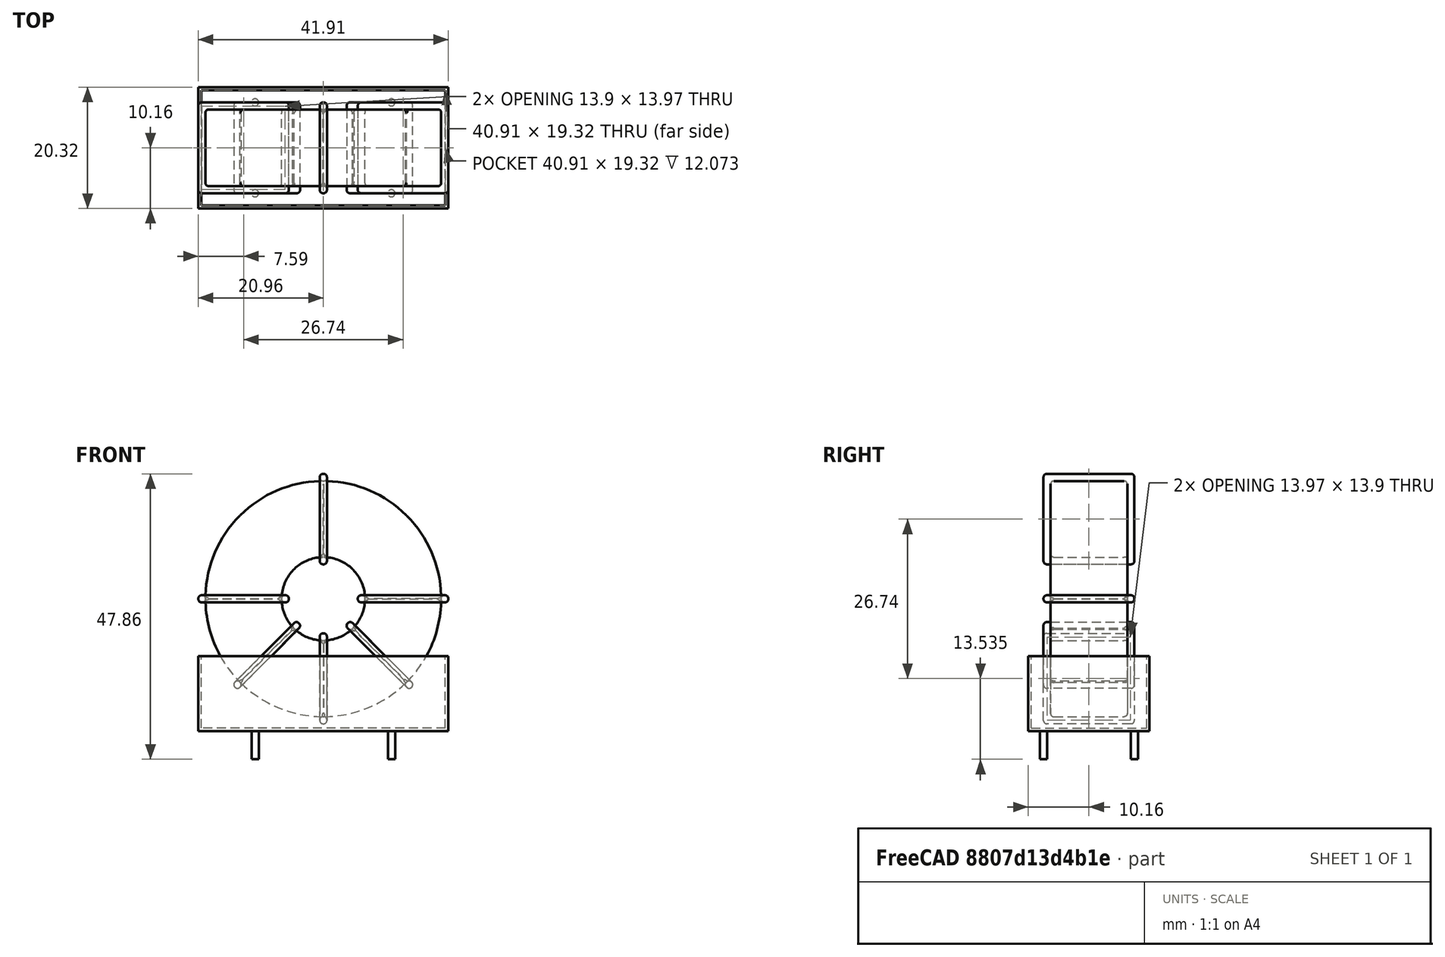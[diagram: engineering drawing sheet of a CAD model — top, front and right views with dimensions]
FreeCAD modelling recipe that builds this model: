
FCSTD DOCUMENT  (FreeCAD 0.16R6712 (Git))
Label: L_CommonMode_Toroid_Vertical_L41.9mm_W20.3mm_Px15.24mm_Py22.86mm_Bourns_8100
License: All rights reserved
LicenseURL: http://en.wikipedia.org/wiki/All_rights_reserved
objects: Sketcher::SketchObject×8, PartDesign::Pad×8, PartDesign::Fillet×5, Spreadsheet::Sheet×1, Part::MultiFuse×1
note: 30 computed .brp shape members not serialized (recipe doc carries the construction recipe); baked Part::Feature solids carry a one-line shape summary decoded from their .brp

FEATURE [Spreadsheet::Sheet] Spreadsheet  label="dimensions"
  cells = A1=Wx; B1(Wx)=41.91; C1(WW)=13.97; D1(iWx)=41.91; A2=Wy; B2(Wy)=15.24; D2(iWy)=20.32; A3=RM; B3(RMx)=15.24; C3(RMy)=22.86; A4=d_wire; B4(d_wire)=1.2; A5=H; B5(H)=31; A6=offsetx; B6(offsetx)=9.524999999999999
FEATURE [Sketcher::SketchObject] Sketch
  Placement = pos=(11.43,-7.62,0) rot=(1,0,0;1.5708rad)
  expr: Placement.Base.x = Spreadsheet.RMy / 2
  expr: Constraints[4] = Spreadsheet.WW / 2
  expr: Placement.Base.y = -Spreadsheet.RMx / 2
  expr: Constraints[0] = Spreadsheet.Wx / 2 - Spreadsheet.d_wire
  expr: Constraints[2] = Spreadsheet.Wx / 2 + Spreadsheet.d_wire + 0.5
  sketch-geometry (2):
    g0: Circle CenterX=0 CenterY=22.655 CenterZ=0 NormalX=0 NormalY=0 NormalZ=1 Radius=19.755
    g1: Circle CenterX=0 CenterY=22.655 CenterZ=0 NormalX=0 NormalY=0 NormalZ=1 Radius=6.985
  constraints (5):
    c: Radius(g0) = 19.755
    c: DistanceX(g-1,g0) = 0
    c: DistanceY(g-1,g0) = 22.655
    c: Coincident(g1,g0)
    c: Radius(g1) = 6.985
FEATURE [PartDesign::Pad] Pad
  Length = 12.84
  Length2 = 100
  Midplane = true
  Placement = pos=(11.43,-7.62,0) rot=(1,0,0;1.5708rad)
  Sketch = -> Sketch
  Type = 0
  expr: Length = Spreadsheet.Wy - 2 * Spreadsheet.d_wire
FEATURE [Sketcher::SketchObject] Sketch001
  Placement = pos=(0,0,0.75) rot=(0,0,1;0rad)
  expr: Constraints[4] = Spreadsheet.RMy
  expr: Constraints[2] = -Spreadsheet.RMx
  expr: Constraints[1] = Spreadsheet.d_wire / 2
  sketch-geometry (4):
    g0: Circle CenterX=0 CenterY=0 CenterZ=0 NormalX=0 NormalY=0 NormalZ=1 Radius=0.6
    g1: Circle CenterX=22.86 CenterY=-15.24 CenterZ=0 NormalX=0 NormalY=0 NormalZ=1 Radius=0.6
    g2: Circle CenterX=0 CenterY=-15.24 CenterZ=0 NormalX=0 NormalY=0 NormalZ=1 Radius=0.6
    g3: Circle CenterX=22.86 CenterY=0 CenterZ=0 NormalX=0 NormalY=0 NormalZ=1 Radius=0.6
  constraints (11):
    c: Equal(g0,g1)
    c: Radius(g0) = 0.6
    c: DistanceY(g-1,g1) = -15.24
    c: Coincident(g0,g-1)
    c: DistanceX(g-1,g1) = 22.86
    c: PointOnObject(g2,g-2)
    c: DistanceY(g-1,g3) = 0
    c: DistanceY(g2,g1) = 0
    c: DistanceX(g3,g1) = 0
    c: Equal(g3,g2)
    c: Equal(g2,g1)
FEATURE [PartDesign::Pad] Pad001
  Length = 5
  Length2 = 0
  Placement = pos=(0,0,0.75) rot=(0,0,1;0rad)
  Reversed = true
  Sketch = -> Sketch001
  Type = 0
FEATURE [PartDesign::Fillet] Fillet
  Base = -> Pad [Edge6,Edge3,Edge2]
  Placement = pos=(11.43,-7.62,0) rot=(1,0,0;1.5708rad)
  Radius = 0.5
FEATURE [Sketcher::SketchObject] Sketch003
  Placement = pos=(11.43,0,22.655) rot=(1,0,0;3.14159rad)
  expr: Placement.Base.x = Spreadsheet.RMy / 2
  expr: Constraints[18] = Spreadsheet.d_wire
  expr: Constraints[16] = Spreadsheet.d_wire
  expr: Constraints[19] = Spreadsheet.d_wire
  expr: Constraints[17] = Spreadsheet.d_wire
  expr: Placement.Base.y = -1 * (Spreadsheet.RMx - Spreadsheet.Wy) / 2
  expr: Constraints[21] = (Spreadsheet.Wx - Spreadsheet.WW) / 2 - Spreadsheet.d_wire
  expr: Constraints[22] = Spreadsheet.Wx / 2 - Spreadsheet.d_wire
  expr: Constraints[43] = Spreadsheet.d_wire
  expr: Constraints[48] = Spreadsheet.Wx - Spreadsheet.d_wire * 2
  expr: Constraints[49] = Spreadsheet.Wy
  expr: Placement.Base.z = Spreadsheet.Wx / 2 + Spreadsheet.d_wire + 0.5
  sketch-geometry (16):
    g0: LineSegment StartX=-5.785 StartY=0 StartZ=0 EndX=-20.955 EndY=0 EndZ=0
    g1: LineSegment StartX=-20.955 StartY=0 StartZ=0 EndX=-20.955 EndY=15.24 EndZ=0
    g2: LineSegment StartX=-20.955 StartY=15.24 StartZ=0 EndX=-5.785 EndY=15.24 EndZ=0
    g3: LineSegment StartX=-5.785 StartY=15.24 StartZ=0 EndX=-5.785 EndY=0 EndZ=0
    g4: LineSegment StartX=-19.755 StartY=14.04 StartZ=0 EndX=-6.985 EndY=14.04 EndZ=0
    g5: LineSegment StartX=-6.985 StartY=14.04 StartZ=0 EndX=-6.985 EndY=1.2 EndZ=0
    g6: LineSegment StartX=-6.985 StartY=1.2 StartZ=0 EndX=-19.755 EndY=1.2 EndZ=0
    g7: LineSegment StartX=-19.755 StartY=1.2 StartZ=0 EndX=-19.755 EndY=14.04 EndZ=0
    g8: LineSegment StartX=5.785 StartY=15.24 StartZ=0 EndX=20.955 EndY=15.24 EndZ=0
    g9: LineSegment StartX=20.955 StartY=15.24 StartZ=0 EndX=20.955 EndY=0 EndZ=0
    g10: LineSegment StartX=20.955 StartY=0 StartZ=0 EndX=5.785 EndY=0 EndZ=0
    g11: LineSegment StartX=5.785 StartY=0 StartZ=0 EndX=5.785 EndY=15.24 EndZ=0
    g12: LineSegment StartX=6.985 StartY=14.04 StartZ=0 EndX=19.755 EndY=14.04 EndZ=0
    g13: LineSegment StartX=19.755 StartY=14.04 StartZ=0 EndX=19.755 EndY=1.2 EndZ=0
    g14: LineSegment StartX=19.755 StartY=1.2 StartZ=0 EndX=6.985 EndY=1.2 EndZ=0
    g15: LineSegment StartX=6.985 StartY=1.2 StartZ=0 EndX=6.985 EndY=14.04 EndZ=0
  constraints (50):
    c: Horizontal(g0)
    c: Coincident(g1,g0)
    c: Vertical(g1)
    c: Coincident(g2,g1)
    c: Horizontal(g2)
    c: Coincident(g3,g2)
    c: Coincident(g3,g0)
    c: Vertical(g3)
    c: Coincident(g4,g5)
    c: Coincident(g5,g6)
    c: Coincident(g6,g7)
    c: Coincident(g7,g4)
    c: Horizontal(g4)
    c: Horizontal(g6)
    c: Vertical(g5)
    c: Vertical(g7)
    c: DistanceX(g1,g4) = 1.2
    c: DistanceY(g4,g1) = 1.2
    c: DistanceX(g5,g0) = 1.2
    c: DistanceY(g0,g5) = 1.2
    c: DistanceY(g-1,g0) = 0
    c: DistanceX(g6,g6) = 12.77
    c: DistanceX(g6,g-1) = 19.755
    c: Coincident(g8,g9)
    c: Coincident(g9,g10)
    c: Coincident(g10,g11)
    c: Coincident(g11,g8)
    c: Horizontal(g8)
    c: Horizontal(g10)
    c: Vertical(g9)
    c: Vertical(g11)
    c: Coincident(g12,g13)
    c: Coincident(g13,g14)
    c: Coincident(g14,g15)
    c: Coincident(g15,g12)
    c: Horizontal(g12)
    c: Horizontal(g14)
    c: Vertical(g13)
    c: Vertical(g15)
    c: DistanceY(g8,g2) = 0
    c: DistanceY(g10,g0) = 0
    c: DistanceY(g14,g5) = 0
    c: DistanceY(g12,g4) = 0
    c: DistanceX(g8,g12) = 1.2
    c: Equal(g8,g2)
    c: Equal(g12,g4)
    c: Equal(g9,g1)
    c: Equal(g13,g7)
    c: DistanceX(g4,g12) = 39.51
    c: DistanceY(g0,g1) = 15.24
FEATURE [PartDesign::Pad] Pad002
  Length = 1.2
  Length2 = 100
  Midplane = true
  Placement = pos=(11.43,0,22.655) rot=(1,0,0;3.14159rad)
  Sketch = -> Sketch003
  Type = 0
  expr: Length = Spreadsheet.d_wire
FEATURE [PartDesign::Fillet] Fillet001
  Base = -> Pad002 [Edge38,Edge41,Edge42,Edge43,Edge29,Edge32,Edge33,Edge34,Edge25,Edge35,Edge36,Edge13,Edge14,Edge15,Edge16,Edge17,Edge18,Edge19,Edge1,Edge2,Edge3,Edge4,Edge5,Edge6,Edge7,Edge37,Edge39,Edge40,Edge20,Edge23,Edge24,Edge21,Edge22,Edge8,Edge9,Edge10,Edge11,Edge12,Edge26,Edge27,+8 more]
  Placement = pos=(11.43,0,22.655) rot=(1,0,0;3.14159rad)
  Radius = 0.564
  expr: Radius = Spreadsheet.d_wire * 0.47
FEATURE [Sketcher::SketchObject] Sketch004
  Placement = pos=(11.43,0,22.655) rot=(0.92388,0,0.382683;3.14159rad)
  expr: Placement.Base.x = Spreadsheet.RMy / 2
  expr: Constraints[18] = Spreadsheet.d_wire
  expr: Constraints[16] = Spreadsheet.d_wire
  expr: Constraints[19] = Spreadsheet.d_wire
  expr: Constraints[17] = Spreadsheet.d_wire
  expr: Placement.Base.y = -1 * (Spreadsheet.RMx - Spreadsheet.Wy) / 2
  expr: Constraints[21] = (Spreadsheet.Wx - Spreadsheet.WW) / 2 - Spreadsheet.d_wire
  expr: Constraints[22] = Spreadsheet.Wx / 2 - Spreadsheet.d_wire
  expr: Constraints[43] = Spreadsheet.d_wire
  expr: Constraints[48] = Spreadsheet.Wx - 2 * Spreadsheet.d_wire
  expr: Constraints[49] = Spreadsheet.Wy
  expr: Placement.Base.z = Spreadsheet.Wx / 2 + Spreadsheet.d_wire + 0.5
  sketch-geometry (16):
    g0: LineSegment StartX=-5.785 StartY=0 StartZ=0 EndX=-20.955 EndY=0 EndZ=0
    g1: LineSegment StartX=-20.955 StartY=0 StartZ=0 EndX=-20.955 EndY=15.24 EndZ=0
    g2: LineSegment StartX=-20.955 StartY=15.24 StartZ=0 EndX=-5.785 EndY=15.24 EndZ=0
    g3: LineSegment StartX=-5.785 StartY=15.24 StartZ=0 EndX=-5.785 EndY=0 EndZ=0
    g4: LineSegment StartX=-19.755 StartY=14.04 StartZ=0 EndX=-6.985 EndY=14.04 EndZ=0
    g5: LineSegment StartX=-6.985 StartY=14.04 StartZ=0 EndX=-6.985 EndY=1.2 EndZ=0
    g6: LineSegment StartX=-6.985 StartY=1.2 StartZ=0 EndX=-19.755 EndY=1.2 EndZ=0
    g7: LineSegment StartX=-19.755 StartY=1.2 StartZ=0 EndX=-19.755 EndY=14.04 EndZ=0
    g8: LineSegment StartX=5.785 StartY=15.24 StartZ=0 EndX=20.955 EndY=15.24 EndZ=0
    g9: LineSegment StartX=20.955 StartY=15.24 StartZ=0 EndX=20.955 EndY=0 EndZ=0
    g10: LineSegment StartX=20.955 StartY=0 StartZ=0 EndX=5.785 EndY=0 EndZ=0
    g11: LineSegment StartX=5.785 StartY=0 StartZ=0 EndX=5.785 EndY=15.24 EndZ=0
    g12: LineSegment StartX=6.985 StartY=14.04 StartZ=0 EndX=19.755 EndY=14.04 EndZ=0
    g13: LineSegment StartX=19.755 StartY=14.04 StartZ=0 EndX=19.755 EndY=1.2 EndZ=0
    g14: LineSegment StartX=19.755 StartY=1.2 StartZ=0 EndX=6.985 EndY=1.2 EndZ=0
    g15: LineSegment StartX=6.985 StartY=1.2 StartZ=0 EndX=6.985 EndY=14.04 EndZ=0
  constraints (50):
    c: Horizontal(g0)
    c: Coincident(g1,g0)
    c: Vertical(g1)
    c: Coincident(g2,g1)
    c: Horizontal(g2)
    c: Coincident(g3,g2)
    c: Coincident(g3,g0)
    c: Vertical(g3)
    c: Coincident(g4,g5)
    c: Coincident(g5,g6)
    c: Coincident(g6,g7)
    c: Coincident(g7,g4)
    c: Horizontal(g4)
    c: Horizontal(g6)
    c: Vertical(g5)
    c: Vertical(g7)
    c: DistanceX(g1,g4) = 1.2
    c: DistanceY(g4,g1) = 1.2
    c: DistanceX(g5,g0) = 1.2
    c: DistanceY(g0,g5) = 1.2
    c: DistanceY(g-1,g0) = 0
    c: DistanceX(g6,g6) = 12.77
    c: DistanceX(g6,g-1) = 19.755
    c: Coincident(g8,g9)
    c: Coincident(g9,g10)
    c: Coincident(g10,g11)
    c: Coincident(g11,g8)
    c: Horizontal(g8)
    c: Horizontal(g10)
    c: Vertical(g9)
    c: Vertical(g11)
    c: Coincident(g12,g13)
    c: Coincident(g13,g14)
    c: Coincident(g14,g15)
    c: Coincident(g15,g12)
    c: Horizontal(g12)
    c: Horizontal(g14)
    c: Vertical(g13)
    c: Vertical(g15)
    c: DistanceY(g8,g2) = 0
    c: DistanceY(g10,g0) = 0
    c: DistanceY(g14,g5) = 0
    c: DistanceY(g12,g4) = 0
    c: DistanceX(g8,g12) = 1.2
    c: Equal(g8,g2)
    c: Equal(g12,g4)
    c: Equal(g9,g1)
    c: Equal(g13,g7)
    c: DistanceX(g4,g12) = 39.51
    c: DistanceY(g0,g1) = 15.24
FEATURE [PartDesign::Pad] Pad003
  Length = 1.2
  Length2 = 100
  Midplane = true
  Placement = pos=(11.43,0,22.655) rot=(0.92388,0,0.382683;3.14159rad)
  Sketch = -> Sketch004
  Type = 0
  expr: Length = Spreadsheet.d_wire
FEATURE [PartDesign::Fillet] Fillet002
  Base = -> Pad003 [Edge38,Edge41,Edge42,Edge43,Edge29,Edge32,Edge33,Edge34,Edge25,Edge35,Edge36,Edge13,Edge14,Edge15,Edge16,Edge17,Edge18,Edge19,Edge1,Edge2,Edge3,Edge4,Edge5,Edge6,Edge7,Edge37,Edge39,Edge40,Edge20,Edge23,Edge24,Edge21,Edge22,Edge8,Edge9,Edge10,Edge11,Edge12,Edge26,Edge27,+8 more]
  Placement = pos=(11.43,0,22.655) rot=(0.92388,0,0.382683;3.14159rad)
  Radius = 0.564
  expr: Radius = Spreadsheet.d_wire * 0.47
FEATURE [Sketcher::SketchObject] Sketch005
  Placement = pos=(11.43,0,22.655) rot=(0.92388,0,-0.382683;3.14159rad)
  expr: Placement.Base.x = Spreadsheet.RMy / 2
  expr: Constraints[18] = Spreadsheet.d_wire
  expr: Constraints[16] = Spreadsheet.d_wire
  expr: Constraints[19] = Spreadsheet.d_wire
  expr: Constraints[17] = Spreadsheet.d_wire
  expr: Placement.Base.y = -1 * (Spreadsheet.RMx - Spreadsheet.Wy) / 2
  expr: Constraints[21] = (Spreadsheet.Wx - Spreadsheet.WW) / 2 - Spreadsheet.d_wire
  expr: Constraints[22] = Spreadsheet.Wx / 2 - Spreadsheet.d_wire
  expr: Constraints[43] = Spreadsheet.d_wire
  expr: Constraints[48] = Spreadsheet.Wx - 2 * Spreadsheet.d_wire
  expr: Constraints[49] = Spreadsheet.Wy
  expr: Placement.Base.z = Spreadsheet.Wx / 2 + Spreadsheet.d_wire + 0.5
  sketch-geometry (16):
    g0: LineSegment StartX=-5.785 StartY=0 StartZ=0 EndX=-20.955 EndY=0 EndZ=0
    g1: LineSegment StartX=-20.955 StartY=0 StartZ=0 EndX=-20.955 EndY=15.24 EndZ=0
    g2: LineSegment StartX=-20.955 StartY=15.24 StartZ=0 EndX=-5.785 EndY=15.24 EndZ=0
    g3: LineSegment StartX=-5.785 StartY=15.24 StartZ=0 EndX=-5.785 EndY=0 EndZ=0
    g4: LineSegment StartX=-19.755 StartY=14.04 StartZ=0 EndX=-6.985 EndY=14.04 EndZ=0
    g5: LineSegment StartX=-6.985 StartY=14.04 StartZ=0 EndX=-6.985 EndY=1.2 EndZ=0
    g6: LineSegment StartX=-6.985 StartY=1.2 StartZ=0 EndX=-19.755 EndY=1.2 EndZ=0
    g7: LineSegment StartX=-19.755 StartY=1.2 StartZ=0 EndX=-19.755 EndY=14.04 EndZ=0
    g8: LineSegment StartX=5.785 StartY=15.24 StartZ=0 EndX=20.955 EndY=15.24 EndZ=0
    g9: LineSegment StartX=20.955 StartY=15.24 StartZ=0 EndX=20.955 EndY=0 EndZ=0
    g10: LineSegment StartX=20.955 StartY=0 StartZ=0 EndX=5.785 EndY=0 EndZ=0
    g11: LineSegment StartX=5.785 StartY=0 StartZ=0 EndX=5.785 EndY=15.24 EndZ=0
    g12: LineSegment StartX=6.985 StartY=14.04 StartZ=0 EndX=19.755 EndY=14.04 EndZ=0
    g13: LineSegment StartX=19.755 StartY=14.04 StartZ=0 EndX=19.755 EndY=1.2 EndZ=0
    g14: LineSegment StartX=19.755 StartY=1.2 StartZ=0 EndX=6.985 EndY=1.2 EndZ=0
    g15: LineSegment StartX=6.985 StartY=1.2 StartZ=0 EndX=6.985 EndY=14.04 EndZ=0
  constraints (50):
    c: Horizontal(g0)
    c: Coincident(g1,g0)
    c: Vertical(g1)
    c: Coincident(g2,g1)
    c: Horizontal(g2)
    c: Coincident(g3,g2)
    c: Coincident(g3,g0)
    c: Vertical(g3)
    c: Coincident(g4,g5)
    c: Coincident(g5,g6)
    c: Coincident(g6,g7)
    c: Coincident(g7,g4)
    c: Horizontal(g4)
    c: Horizontal(g6)
    c: Vertical(g5)
    c: Vertical(g7)
    c: DistanceX(g1,g4) = 1.2
    c: DistanceY(g4,g1) = 1.2
    c: DistanceX(g5,g0) = 1.2
    c: DistanceY(g0,g5) = 1.2
    c: DistanceY(g-1,g0) = 0
    c: DistanceX(g6,g6) = 12.77
    c: DistanceX(g6,g-1) = 19.755
    c: Coincident(g8,g9)
    c: Coincident(g9,g10)
    c: Coincident(g10,g11)
    c: Coincident(g11,g8)
    c: Horizontal(g8)
    c: Horizontal(g10)
    c: Vertical(g9)
    c: Vertical(g11)
    c: Coincident(g12,g13)
    c: Coincident(g13,g14)
    c: Coincident(g14,g15)
    c: Coincident(g15,g12)
    c: Horizontal(g12)
    c: Horizontal(g14)
    c: Vertical(g13)
    c: Vertical(g15)
    c: DistanceY(g8,g2) = 0
    c: DistanceY(g10,g0) = 0
    c: DistanceY(g14,g5) = 0
    c: DistanceY(g12,g4) = 0
    c: DistanceX(g8,g12) = 1.2
    c: Equal(g8,g2)
    c: Equal(g12,g4)
    c: Equal(g9,g1)
    c: Equal(g13,g7)
    c: DistanceX(g4,g12) = 39.51
    c: DistanceY(g0,g1) = 15.24
FEATURE [PartDesign::Pad] Pad004
  Length = 1.2
  Length2 = 100
  Midplane = true
  Placement = pos=(11.43,0,22.655) rot=(0.92388,0,-0.382683;3.14159rad)
  Sketch = -> Sketch005
  Type = 0
  expr: Length = Spreadsheet.d_wire
FEATURE [PartDesign::Fillet] Fillet003
  Base = -> Pad004 [Edge38,Edge41,Edge42,Edge43,Edge29,Edge32,Edge33,Edge34,Edge25,Edge35,Edge36,Edge13,Edge14,Edge15,Edge16,Edge17,Edge18,Edge19,Edge1,Edge2,Edge3,Edge4,Edge5,Edge6,Edge7,Edge37,Edge39,Edge40,Edge20,Edge23,Edge24,Edge21,Edge22,Edge8,Edge9,Edge10,Edge11,Edge12,Edge26,Edge27,+8 more]
  Placement = pos=(11.43,0,22.655) rot=(0.92388,0,-0.382683;3.14159rad)
  Radius = 0.564
  expr: Radius = Spreadsheet.d_wire * 0.47
FEATURE [Sketcher::SketchObject] Sketch006
  Placement = pos=(11.43,0,22.655) rot=(0.707107,0,0.707107;3.14159rad)
  expr: Placement.Base.x = Spreadsheet.RMy / 2
  expr: Constraints[18] = Spreadsheet.d_wire
  expr: Constraints[16] = Spreadsheet.d_wire
  expr: Constraints[19] = Spreadsheet.d_wire
  expr: Constraints[17] = Spreadsheet.d_wire
  expr: Placement.Base.y = -1 * (Spreadsheet.RMx - Spreadsheet.Wy) / 2
  expr: Constraints[21] = (Spreadsheet.Wx - Spreadsheet.WW) / 2 - Spreadsheet.d_wire
  expr: Constraints[22] = Spreadsheet.Wx / 2 - Spreadsheet.d_wire
  expr: Constraints[43] = Spreadsheet.d_wire
  expr: Constraints[48] = Spreadsheet.Wx - Spreadsheet.d_wire * 2
  expr: Constraints[49] = Spreadsheet.Wy
  expr: Placement.Base.z = Spreadsheet.Wx / 2 + Spreadsheet.d_wire + 0.5
  sketch-geometry (16):
    g0: LineSegment StartX=-5.785 StartY=0 StartZ=0 EndX=-20.955 EndY=0 EndZ=0
    g1: LineSegment StartX=-20.955 StartY=0 StartZ=0 EndX=-20.955 EndY=15.24 EndZ=0
    g2: LineSegment StartX=-20.955 StartY=15.24 StartZ=0 EndX=-5.785 EndY=15.24 EndZ=0
    g3: LineSegment StartX=-5.785 StartY=15.24 StartZ=0 EndX=-5.785 EndY=0 EndZ=0
    g4: LineSegment StartX=-19.755 StartY=14.04 StartZ=0 EndX=-6.985 EndY=14.04 EndZ=0
    g5: LineSegment StartX=-6.985 StartY=14.04 StartZ=0 EndX=-6.985 EndY=1.2 EndZ=0
    g6: LineSegment StartX=-6.985 StartY=1.2 StartZ=0 EndX=-19.755 EndY=1.2 EndZ=0
    g7: LineSegment StartX=-19.755 StartY=1.2 StartZ=0 EndX=-19.755 EndY=14.04 EndZ=0
    g8: LineSegment StartX=5.785 StartY=15.24 StartZ=0 EndX=20.955 EndY=15.24 EndZ=0
    g9: LineSegment StartX=20.955 StartY=15.24 StartZ=0 EndX=20.955 EndY=0 EndZ=0
    g10: LineSegment StartX=20.955 StartY=0 StartZ=0 EndX=5.785 EndY=0 EndZ=0
    g11: LineSegment StartX=5.785 StartY=0 StartZ=0 EndX=5.785 EndY=15.24 EndZ=0
    g12: LineSegment StartX=6.985 StartY=14.04 StartZ=0 EndX=19.755 EndY=14.04 EndZ=0
    g13: LineSegment StartX=19.755 StartY=14.04 StartZ=0 EndX=19.755 EndY=1.2 EndZ=0
    g14: LineSegment StartX=19.755 StartY=1.2 StartZ=0 EndX=6.985 EndY=1.2 EndZ=0
    g15: LineSegment StartX=6.985 StartY=1.2 StartZ=0 EndX=6.985 EndY=14.04 EndZ=0
  constraints (50):
    c: Horizontal(g0)
    c: Coincident(g1,g0)
    c: Vertical(g1)
    c: Coincident(g2,g1)
    c: Horizontal(g2)
    c: Coincident(g3,g2)
    c: Coincident(g3,g0)
    c: Vertical(g3)
    c: Coincident(g4,g5)
    c: Coincident(g5,g6)
    c: Coincident(g6,g7)
    c: Coincident(g7,g4)
    c: Horizontal(g4)
    c: Horizontal(g6)
    c: Vertical(g5)
    c: Vertical(g7)
    c: DistanceX(g1,g4) = 1.2
    c: DistanceY(g4,g1) = 1.2
    c: DistanceX(g5,g0) = 1.2
    c: DistanceY(g0,g5) = 1.2
    c: DistanceY(g-1,g0) = 0
    c: DistanceX(g6,g6) = 12.77
    c: DistanceX(g6,g-1) = 19.755
    c: Coincident(g8,g9)
    c: Coincident(g9,g10)
    c: Coincident(g10,g11)
    c: Coincident(g11,g8)
    c: Horizontal(g8)
    c: Horizontal(g10)
    c: Vertical(g9)
    c: Vertical(g11)
    c: Coincident(g12,g13)
    c: Coincident(g13,g14)
    c: Coincident(g14,g15)
    c: Coincident(g15,g12)
    c: Horizontal(g12)
    c: Horizontal(g14)
    c: Vertical(g13)
    c: Vertical(g15)
    c: DistanceY(g8,g2) = 0
    c: DistanceY(g10,g0) = 0
    c: DistanceY(g14,g5) = 0
    c: DistanceY(g12,g4) = 0
    c: DistanceX(g8,g12) = 1.2
    c: Equal(g8,g2)
    c: Equal(g12,g4)
    c: Equal(g9,g1)
    c: Equal(g13,g7)
    c: DistanceX(g4,g12) = 39.51
    c: DistanceY(g0,g1) = 15.24
FEATURE [PartDesign::Pad] Pad005
  Length = 1.2
  Length2 = 100
  Midplane = true
  Placement = pos=(11.43,0,22.655) rot=(0.707107,0,0.707107;3.14159rad)
  Sketch = -> Sketch006
  Type = 0
  expr: Length = Spreadsheet.d_wire
FEATURE [PartDesign::Fillet] Fillet004
  Base = -> Pad005 [Edge38,Edge41,Edge42,Edge43,Edge29,Edge32,Edge33,Edge34,Edge25,Edge35,Edge36,Edge13,Edge14,Edge15,Edge16,Edge17,Edge18,Edge19,Edge1,Edge2,Edge3,Edge4,Edge5,Edge6,Edge7,Edge37,Edge39,Edge40,Edge20,Edge23,Edge24,Edge21,Edge22,Edge8,Edge9,Edge10,Edge11,Edge12,Edge26,Edge27,+8 more]
  Placement = pos=(11.43,0,22.655) rot=(0.707107,0,0.707107;3.14159rad)
  Radius = 0.564
  expr: Radius = Spreadsheet.d_wire * 0.47
FEATURE [Sketcher::SketchObject] Sketch007
  Placement = pos=(11.43,0,0.5) rot=(0,0,1;0rad)
  expr: Placement.Base.x = Spreadsheet.RMy / 2
  expr: Placement.Base.z = 0.5
  expr: Constraints[11] = Spreadsheet.iWx / 2
  expr: Constraints[10] = (Spreadsheet.iWy - Spreadsheet.RMx) / 2
  expr: Constraints[9] = Spreadsheet.iWy
  expr: Constraints[8] = Spreadsheet.iWx
  sketch-geometry (4):
    g0: LineSegment StartX=-20.955 StartY=2.54 StartZ=0 EndX=20.955 EndY=2.54 EndZ=0
    g1: LineSegment StartX=20.955 StartY=2.54 StartZ=0 EndX=20.955 EndY=-17.78 EndZ=0
    g2: LineSegment StartX=20.955 StartY=-17.78 StartZ=0 EndX=-20.955 EndY=-17.78 EndZ=0
    g3: LineSegment StartX=-20.955 StartY=-17.78 StartZ=0 EndX=-20.955 EndY=2.54 EndZ=0
  constraints (12):
    c: Coincident(g0,g1)
    c: Coincident(g1,g2)
    c: Coincident(g2,g3)
    c: Coincident(g3,g0)
    c: Horizontal(g0)
    c: Horizontal(g2)
    c: Vertical(g1)
    c: Vertical(g3)
    c: DistanceX(g0,g0) = 41.91
    c: DistanceY(g3,g3) = 20.32
    c: DistanceY(g-1,g0) = 2.54
    c: DistanceX(g0,g-1) = 20.955
FEATURE [PartDesign::Pad] Pad006
  Length = 0.5
  Length2 = 100
  Placement = pos=(11.43,0,0.5) rot=(0,0,1;0rad)
  Sketch = -> Sketch007
  Type = 0
FEATURE [Sketcher::SketchObject] Sketch008
  Placement = pos=(11.43,0,0.5) rot=(0,0,1;0rad)
  expr: Placement.Base.x = Spreadsheet.RMy / 2
  expr: Constraints[8] = Spreadsheet.iWx
  expr: Constraints[9] = Spreadsheet.iWy
  expr: Constraints[10] = (Spreadsheet.iWy - Spreadsheet.RMx) / 2
  expr: Placement.Base.z = 0.5
  expr: Constraints[21] = 0.5
  expr: Constraints[11] = Spreadsheet.iWx / 2
  sketch-geometry (8):
    g0: LineSegment StartX=-20.955 StartY=2.54 StartZ=0 EndX=20.955 EndY=2.54 EndZ=0
    g1: LineSegment StartX=20.955 StartY=2.54 StartZ=0 EndX=20.955 EndY=-17.78 EndZ=0
    g2: LineSegment StartX=20.955 StartY=-17.78 StartZ=0 EndX=-20.955 EndY=-17.78 EndZ=0
    g3: LineSegment StartX=-20.955 StartY=-17.78 StartZ=0 EndX=-20.955 EndY=2.54 EndZ=0
    g4: LineSegment StartX=-20.455 StartY=2.04 StartZ=0 EndX=20.455 EndY=2.04 EndZ=0
    g5: LineSegment StartX=20.455 StartY=2.04 StartZ=0 EndX=20.455 EndY=-17.28 EndZ=0
    g6: LineSegment StartX=20.455 StartY=-17.28 StartZ=0 EndX=-20.455 EndY=-17.28 EndZ=0
    g7: LineSegment StartX=-20.455 StartY=-17.28 StartZ=0 EndX=-20.455 EndY=2.04 EndZ=0
  constraints (24):
    c: Coincident(g0,g1)
    c: Coincident(g1,g2)
    c: Coincident(g2,g3)
    c: Coincident(g3,g0)
    c: Horizontal(g0)
    c: Horizontal(g2)
    c: Vertical(g1)
    c: Vertical(g3)
    c: DistanceX(g0,g0) = 41.91
    c: DistanceY(g3,g3) = 20.32
    c: DistanceY(g-1,g0) = 2.54
    c: DistanceX(g0,g-1) = 20.955
    c: Coincident(g4,g5)
    c: Coincident(g5,g6)
    c: Coincident(g6,g7)
    c: Coincident(g7,g4)
    c: Horizontal(g4)
    c: Horizontal(g6)
    c: Vertical(g5)
    c: Vertical(g7)
    c: DistanceX(g5,g1) = 0.5
    c: DistanceY(g1,g5) = 0.5
    c: DistanceX(g0,g4) = 0.5
    c: DistanceY(g4,g0) = 0.5
FEATURE [PartDesign::Pad] Pad007
  Length = 12.573
  Length2 = 100
  Placement = pos=(11.43,0,0.5) rot=(0,0,1;0rad)
  Sketch = -> Sketch008
  Type = 0
  expr: Length = Spreadsheet.Wx * 0.3
FEATURE [Part::MultiFuse] Pad001_mp_cp  label="L_CommonMode_Toroid_Vertical_L41.9mm_W20.3mm_Px15.24mm_Py22.86mm_Bourns_8100"
  Shapes = -> [Pad001,Fillet,Fillet001,Fillet002,Fillet003,Fillet004,Pad006,Pad007]
